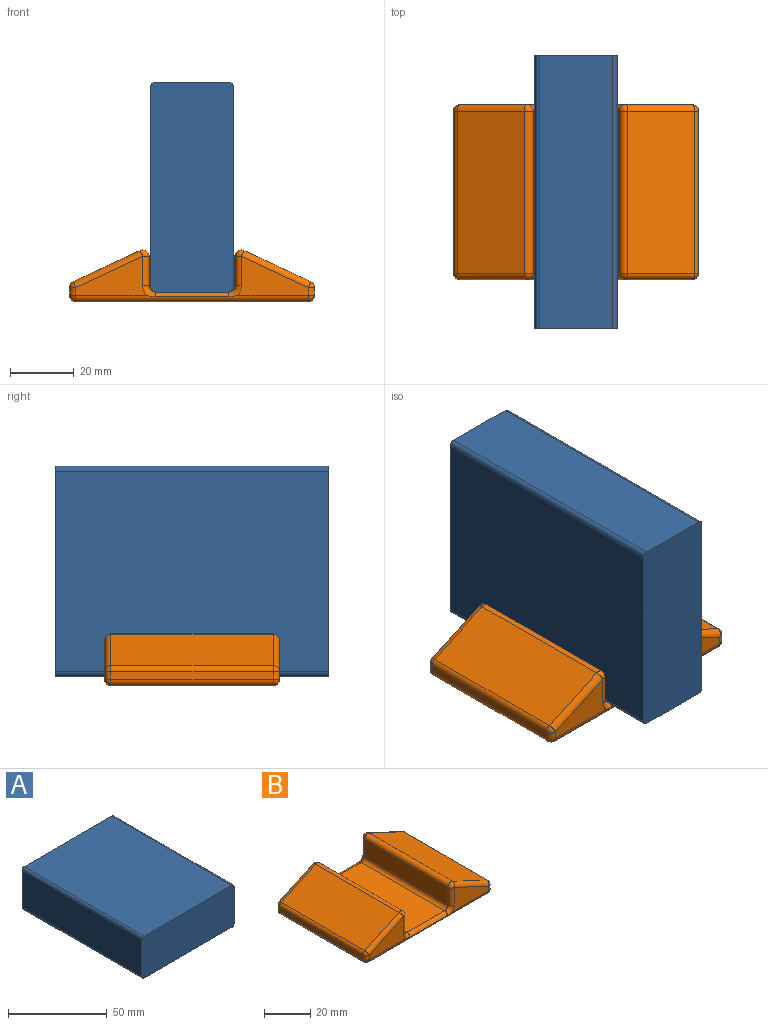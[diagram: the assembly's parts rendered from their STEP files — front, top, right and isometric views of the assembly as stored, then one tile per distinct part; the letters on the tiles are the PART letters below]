
ASSEMBLY  parts=2 mates=1
PART A: 10 faces, bbox 66x86x26 mm
  f0: plane 66x26mm, normal (0,-1,0), area 1714.1mm2, adj f1,f3,f4,f5,f6,f7,f8,f9
  f1: plane 86x23mm, normal (1,0,0), area 1978mm2, adj f0,f2,f6,f8
  f2: plane 66x26mm, normal (0,1,0), area 1714.1mm2, adj f1,f3,f4,f5,f6,f7,f8,f9
  f3: plane 86x23mm, normal (-1,0,0), area 1978mm2, adj f0,f2,f7,f9
  f4: plane 86x63mm, normal (0,0,1), area 5418mm2, adj f0,f2,f8,f9
  f5: plane 86x63mm, normal (0,0,-1), area 5418mm2, adj f0,f2,f6,f7
  f6: cylinder r=1.5mm len=86mm, axis (0,1,0), area 202.6mm2, adj f0,f1,f2,f5
  f7: cylinder r=1.5mm len=86mm, axis (0,-1,0), area 202.6mm2, adj f0,f2,f3,f5
  f8: cylinder r=1.5mm len=86mm, axis (0,-1,0), area 202.6mm2, adj f0,f1,f2,f4
  f9: cylinder r=1.5mm len=86mm, axis (0,1,0), area 202.6mm2, adj f0,f2,f3,f4
PART B: 52 faces, bbox 77x55x17.1 mm
  f0: plane 22.35x12.27mm, normal (0,1,0), area 156.1mm2, adj f12,f18,f20,f23,f36
  f1: plane 22.35x12.27mm, normal (0,-1,0), area 156.1mm2, adj f29,f45,f46,f50,f51
  f2: plane 22.35x12.27mm, normal (0,-1,0), area 156.1mm2, adj f16,f32,f33,f42,f46
  f3: plane 22.35x12.27mm, normal (0,1,0), area 156.1mm2, adj f19,f27,f36,f37,f43
  f4: plane 51x23mm, normal (0,0,1), area 1173mm2, adj f34,f35,f47,f48
  f5: plane 73x51mm, normal (0,0,-1), area 3723mm2, adj f30,f31,f36,f46
  f6: plane 51x9.27mm, normal (-1,0,0), area 472.8mm2, adj f37,f44,f48,f51
  f7: plane 51x2.48mm, normal (1,0,0), area 126.4mm2, adj f19,f28,f29,f30
  f8: plane 51x21mm, normal (0.42,0,0.91), area 1181.7mm2, adj f27,f28,f44,f45
  f9: plane 51x9.27mm, normal (1,0,0), area 472.8mm2, adj f17,f18,f33,f34
  f10: plane 51x2.48mm, normal (-1,0,0), area 126.4mm2, adj f15,f20,f31,f32
  f11: plane 51x21mm, normal (-0.42,0,0.91), area 1181.7mm2, adj f12,f15,f16,f17
  f12: cylinder r=2mm len=21.85mm, axis (0.91,0,0.42), area 72.8mm2, adj f0,f11,f13,f14
  f13: sphere r=2mm, area 8mm2, adj f12,f17,f18
  f14: sphere r=2mm, area 4.5mm2, adj f12,f15,f20
  f15: cylinder r=2mm len=51mm, axis (0,1,0), area 115.7mm2, adj f10,f11,f14,f21
  f16: cylinder r=2mm len=21.85mm, axis (-0.91,0,-0.42), area 72.8mm2, adj f2,f11,f21,f22
  f17: cylinder r=2mm len=51mm, axis (0,-1,0), area 204.7mm2, adj f9,f11,f13,f22
  f18: cylinder r=2mm len=9.27mm, axis (0,0,-1), area 29.1mm2, adj f0,f9,f13,f23
  f19: cylinder r=2mm len=2.48mm, axis (0,0,-1), area 7.8mm2, adj f3,f7,f25,f26
  f20: cylinder r=2mm len=2.48mm, axis (0,0,1), area 7.8mm2, adj f0,f10,f14,f24
  f21: sphere r=2mm, area 4.5mm2, adj f15,f16,f32
  f22: sphere r=2mm, area 8mm2, adj f16,f17,f33
  f23: torus R=4mm, axis (0,-1,0), area 12.5mm2, adj f0,f18,f34,f35,f36
  f24: sphere r=2mm, area 6.3mm2, adj f20,f31,f36
  f25: sphere r=2mm, area 4.5mm2, adj f19,f27,f28
  f26: sphere r=2mm, area 6.3mm2, adj f19,f30,f36
  f27: cylinder r=2mm len=21.85mm, axis (-0.91,0,0.42), area 72.8mm2, adj f3,f8,f25,f38
  f28: cylinder r=2mm len=51mm, axis (0,-1,0), area 115.7mm2, adj f7,f8,f25,f39
  f29: cylinder r=2mm len=2.48mm, axis (0,0,1), area 7.8mm2, adj f1,f7,f39,f40
  f30: cylinder r=2mm len=51mm, axis (0,1,0), area 160.2mm2, adj f5,f7,f26,f40
  f31: cylinder r=2mm len=51mm, axis (0,-1,0), area 160.2mm2, adj f5,f10,f24,f41
  f32: cylinder r=2mm len=2.48mm, axis (0,0,-1), area 7.8mm2, adj f2,f10,f21,f41
  f33: cylinder r=2mm len=9.27mm, axis (0,0,1), area 29.1mm2, adj f2,f9,f22,f42
  f34: cylinder r=2mm len=51mm, axis (0,1,0), area 160.2mm2, adj f4,f9,f23,f42
  f35: cylinder r=2mm len=23mm, axis (1,0,0), area 60.6mm2, adj f4,f23,f36,f43
  f36: cylinder r=2mm len=73mm, axis (-1,0,0), area 215.9mm2, adj f0,f3,f5,f23,f24,f26,f35,f43
  f37: cylinder r=2mm len=9.27mm, axis (0,0,1), area 29.1mm2, adj f3,f6,f38,f43
  f38: sphere r=2mm, area 8mm2, adj f27,f37,f44
  f39: sphere r=2mm, area 4.5mm2, adj f28,f29,f45
  f40: sphere r=2mm, area 6.3mm2, adj f29,f30,f46
  f41: sphere r=2mm, area 6.3mm2, adj f31,f32,f46
  f42: torus R=4mm, axis (0,-1,0), area 12.5mm2, adj f2,f33,f34,f46,f47
  f43: torus R=4mm, axis (0,-1,0), area 12.5mm2, adj f3,f35,f36,f37,f48
  f44: cylinder r=2mm len=51mm, axis (0,1,0), area 204.7mm2, adj f6,f8,f38,f49
  f45: cylinder r=2mm len=21.85mm, axis (0.91,0,-0.42), area 72.8mm2, adj f1,f8,f39,f49
  f46: cylinder r=2mm len=73mm, axis (1,0,0), area 215.9mm2, adj f1,f2,f5,f40,f41,f42,f47,f50
  f47: cylinder r=2mm len=23mm, axis (-1,0,0), area 60.6mm2, adj f4,f42,f46,f50
  f48: cylinder r=2mm len=51mm, axis (0,-1,0), area 160.2mm2, adj f4,f6,f43,f50
  f49: sphere r=2mm, area 8mm2, adj f44,f45,f51
  f50: torus R=4mm, axis (0,-1,0), area 12.5mm2, adj f1,f46,f47,f48,f51
  f51: cylinder r=2mm len=9.27mm, axis (0,0,-1), area 29.1mm2, adj f1,f6,f49,f50
PLACE A rot(axis=(0,1,0),90deg) t=(62.29,-19.79,36)mm
PLACE B at identity fixed
MATE fastened A.f1 <-> B.f4  axis (0,0,-1) through (75.29,-19.79,3)mm
